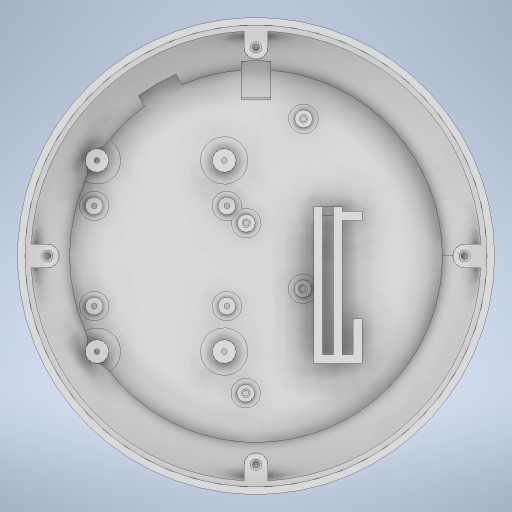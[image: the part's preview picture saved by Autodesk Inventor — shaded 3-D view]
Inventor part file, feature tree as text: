
AUTODESK INVENTOR PART (.ipt)
format: ipt  version: 2023 (Build 270158000, 158)  size: 754,688 bytes
history: native  units: mm
features: extrude x12, sketch x12, other x3, chamfer x3, fillet x2, revolve x1, shell x1, hole x1, pattern_circular x1
ambient origin geometry x8: Origin, YZ Plane, XZ Plane, XY Plane, X Axis, Y Axis, Z Axis, Center Point
bodies: Body1 (feature_tree)
feature tree (36):
  other  "솔리드1"
  revolve  "회전1"
  shell  "쉘1"  Thickness=120.0mm
  extrude  "돌출10"  Depth=140.0mm
  extrude  "돌출11"  Depth=60.0mm
  chamfer  "모따기1"  Distance=130.0mm
  hole  "구멍5"  [1 undecoded]
  pattern_circular  "원형 패턴1"  Angle=360.0deg  [1 undecoded]
  sketch  "스케치24"
  extrude  "돌출12"  Depth=4.0mm
  extrude  "돌출13"  Depth=5.0mm TaperAngle=0.0deg
  other  "작업 평면3"
  extrude  "돌출14"  Depth=155.0mm
  other  "작업 평면4"
  sketch  "스케치26"
  extrude  "돌출15"  Depth=8.0mm
  extrude  "돌출16"  Depth=70.0mm
  extrude  "돌출17"  Depth=10.0mm TaperAngle=0.0deg
  extrude  "돌출18"  Depth=8.25mm TaperAngle=45.0deg
  extrude  "돌출19"  Depth=40.0mm TaperAngle=360.0deg
  chamfer  "모따기2"  Distance=50.7mm
  fillet  "모깎기2"  Radius=38.7mm
  fillet  "모깎기3"  Radius=32.0mm
  extrude  "돌출20"  Depth=2.0mm
  chamfer  "모따기3"  Distance=33.6mm
  extrude  "돌출21"  Depth=44.5mm
  sketch  "스케치1"
  sketch  "스케치21"
  sketch  "스케치22"
  sketch  "스케치23"
  sketch  "스케치25"
  sketch  "스케치27"
  sketch  "스케치28"
  sketch  "스케치30"
  sketch  "스케치31"
  sketch  "스케치32"
note: 2 required parameter values undecoded (feature->parameter linkage not recoverable at this tier; creation-order binding heuristic only, values carry confidence <= 0.55)
